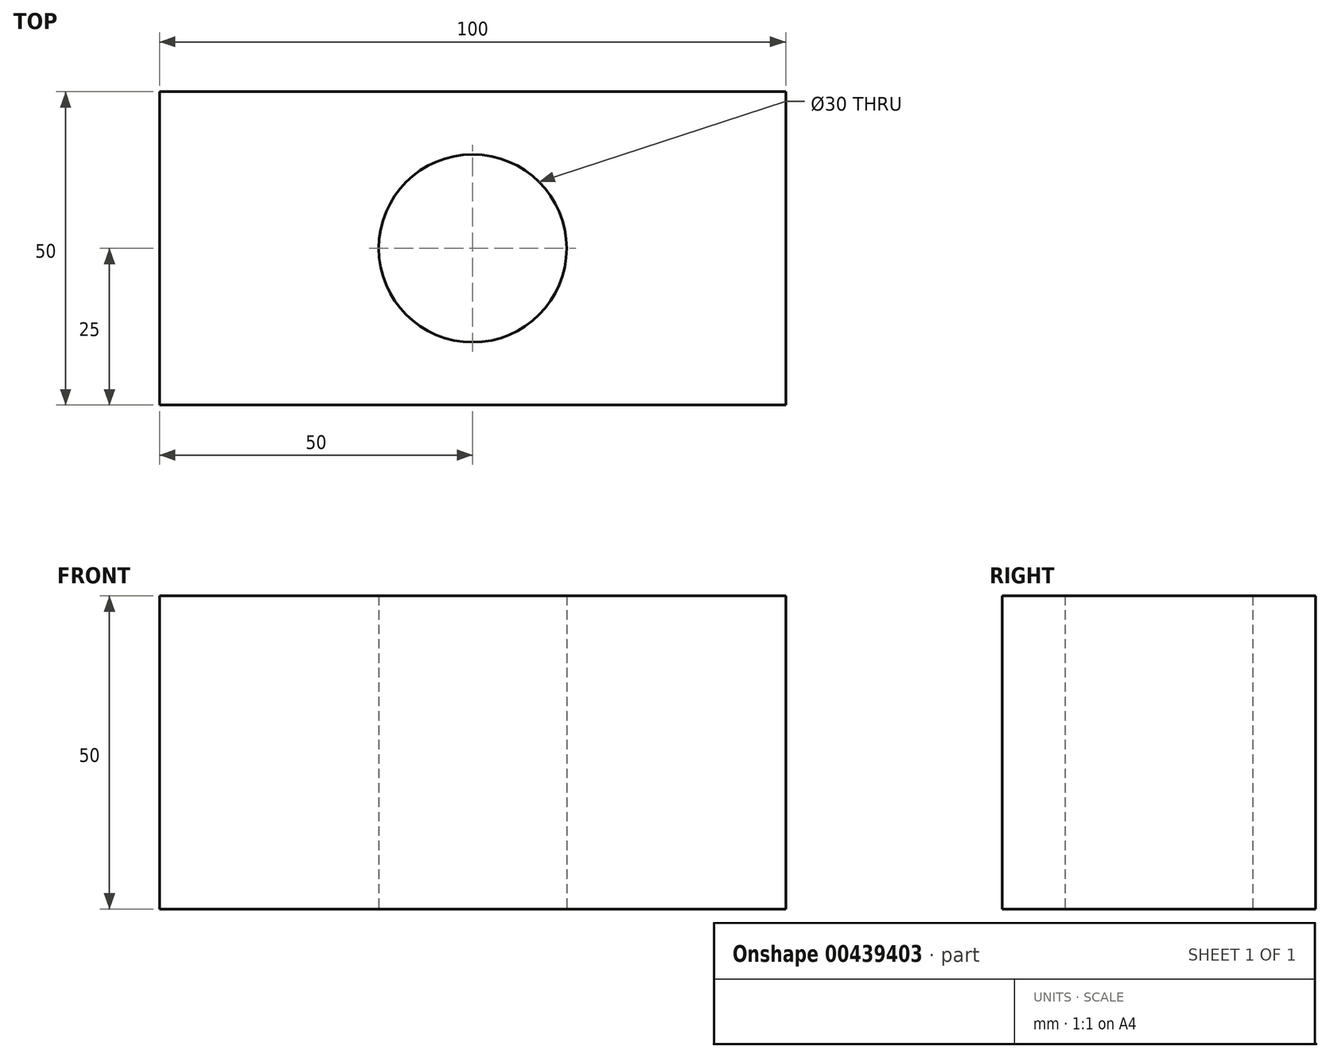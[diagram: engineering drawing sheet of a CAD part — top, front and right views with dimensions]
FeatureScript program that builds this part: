
annotation { "Feature Type Name" : "Feature", "Feature Type Description" : "" }
export const myFeature = defineFeature(function(context is Context, id is Id, definition is map)
    precondition{}
    {
        {
            var Q0;
            Q0=qCreatedBy(makeId("Top.planeOp"),FACE);
            var sketch = newSketch(context, id + "F0", { "sketchPlane" : qUnion([Q0])});
            skLineSegment(sketch, "E0.bottom", {"start": v(-50, 25) * mm, "end": v(50, 25) * mm});
            skLineSegment(sketch, "E0.top", {"start": v(-50, -25) * mm, "end": v(50, -25) * mm});
            skLineSegment(sketch, "E0.left", {"start": v(-50, 25) * mm, "end": v(-50, -25) * mm});
            skLineSegment(sketch, "E0.right", {"start": v(50, 25) * mm, "end": v(50, -25) * mm});
            skPoint(sketch, "E0.middle", {"position": v(0, 0) * mm});
            skCircle(sketch, "E1", {"center": v(0, 0) * mm, "radius": 15 * mm});
            skSolve(sketch);
        }
        {
            var Q0;
            Q0=makeQuery(id+"F0.imprint","IMPRINT",FACE,{"disambiguationData":[TD([[makeQuery(id+"F0.imprint","IMPRINT",EDGE,{"derivedFrom":sQuery(id+"F0.wireOp",EDGE,"E0.bottom")}),-1.0]])]});
            extrude(context, id + "F1", {"entities" : qUnion([Q0]), "depth" : 50 * mm});
        }
        {
            var Q0;
            Q0=makeQuery(id+"F1.opExtrude","SWEPT_FACE",FACE,{"disambiguationData":[OSD([sQuery(id+"F0.wireOp",EDGE,"E0.top")])]});
            var sketch = newSketch(context, id + "F2", { "sketchPlane" : qUnion([Q0])});
            skCircle(sketch, "E2", {"center": v(-12.03, 23.5) * mm, "radius": 7.5 * mm});
            skSolve(sketch);
        }
    });
